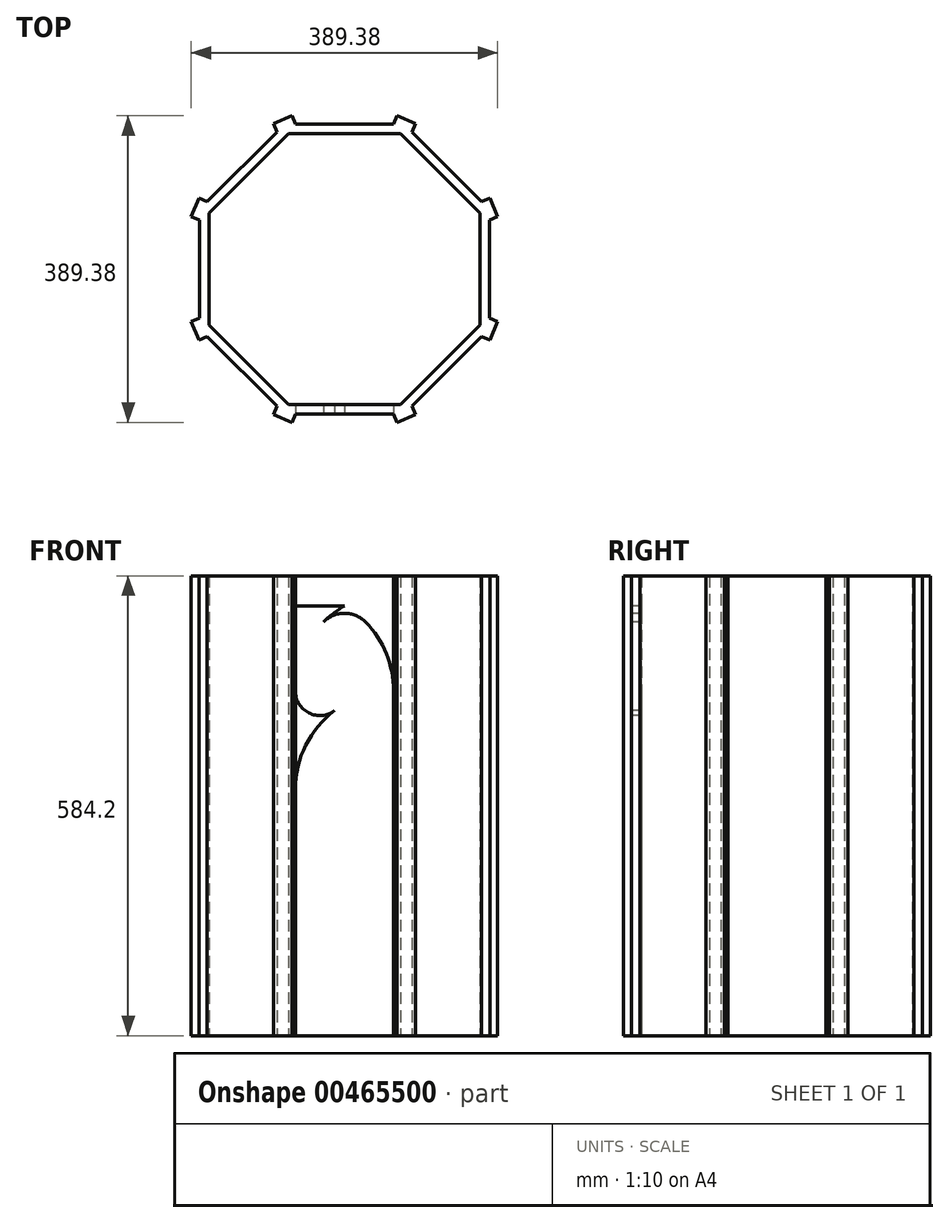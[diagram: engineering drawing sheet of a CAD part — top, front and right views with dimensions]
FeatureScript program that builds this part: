
annotation { "Feature Type Name" : "Feature", "Feature Type Description" : "" }
export const myFeature = defineFeature(function(context is Context, id is Id, definition is map)
    precondition{}
    {
        {
            var Q0;
            Q0=qCreatedBy(makeId("Top.planeOp"),FACE);
            var sketch = newSketch(context, id + "F0", { "sketchPlane" : qUnion([Q0])});
            skLineSegment(sketch, "E0.bottom", {"start": v(76.2, 183.96) * mm, "end": v(-76.2, 183.96) * mm});
            skLineSegment(sketch, "E0.top", {"start": v(76.2, -183.96) * mm, "end": v(-76.2, -183.96) * mm});
            skLineSegment(sketch, "E0.left", {"start": v(183.96, 76.2) * mm, "end": v(183.96, -76.2) * mm});
            skLineSegment(sketch, "E0.right", {"start": v(-183.96, 76.2) * mm, "end": v(-183.96, -76.2) * mm});
            skPoint(sketch, "E0.middle", {"position": v(0, 0) * mm});
            skLineSegment(sketch, "E1", {"start": v(-183.96, 76.2) * mm, "end": v(-76.2, 183.96) * mm});
            skLineSegment(sketch, "E2", {"start": v(-76.2, 183.96) * mm, "end": v(76.2, 183.96) * mm});
            skLineSegment(sketch, "E3", {"start": v(76.2, 183.96) * mm, "end": v(183.96, 76.2) * mm});
            skLineSegment(sketch, "E4", {"start": v(183.96, -76.2) * mm, "end": v(76.2, -183.96) * mm});
            skLineSegment(sketch, "E5", {"start": v(-76.2, -183.96) * mm, "end": v(-183.96, -76.2) * mm});
            skLineSegment(sketch, "E6", {"start": v(-183.96, -76.2) * mm, "end": v(-183.96, 76.2) * mm});
            skPoint(sketch, "E7.orphan", {"position": v(183.96, 183.96) * mm});
            skPoint(sketch, "E8.orphan", {"position": v(183.96, -183.96) * mm});
            skPoint(sketch, "E9.orphan", {"position": v(-183.96, -183.96) * mm});
            skLineSegment(sketch, "E10", {"start": v(-183.96, -62.45) * mm, "end": v(-194.69, -66.9) * mm});
            skLineSegment(sketch, "E11", {"start": v(-194.69, -66.9) * mm, "end": v(-184.97, -90.36) * mm});
            skLineSegment(sketch, "E12", {"start": v(-184.97, -90.36) * mm, "end": v(-174.24, -85.92) * mm});
            skLineSegment(sketch, "E13", {"start": v(-183.96, -76.2) * mm, "end": v(-224.47, -92.98) * mm, "construction": true});
            skPoint(sketch, "E14", {"position": v(-189.83, -78.63) * mm});
            skLineSegment(sketch, "E15.1.0", {"start": v(-184.97, 90.36) * mm, "end": v(-194.69, 66.9) * mm});
            skLineSegment(sketch, "E15.1.1", {"start": v(-194.69, 66.9) * mm, "end": v(-183.96, 62.45) * mm});
            skLineSegment(sketch, "E15.1.2", {"start": v(-174.24, 85.92) * mm, "end": v(-184.97, 90.36) * mm});
            skLineSegment(sketch, "E15.2.0", {"start": v(-66.9, 194.69) * mm, "end": v(-90.36, 184.97) * mm});
            skLineSegment(sketch, "E15.2.1", {"start": v(-90.36, 184.97) * mm, "end": v(-85.92, 174.24) * mm});
            skLineSegment(sketch, "E15.2.2", {"start": v(-62.45, 183.96) * mm, "end": v(-66.9, 194.69) * mm});
            skLineSegment(sketch, "E15.3.0", {"start": v(90.36, 184.97) * mm, "end": v(66.9, 194.69) * mm});
            skLineSegment(sketch, "E15.3.1", {"start": v(66.9, 194.69) * mm, "end": v(62.45, 183.96) * mm});
            skLineSegment(sketch, "E15.3.2", {"start": v(85.92, 174.24) * mm, "end": v(90.36, 184.97) * mm});
            skLineSegment(sketch, "E15.4.0", {"start": v(194.69, 66.9) * mm, "end": v(184.97, 90.36) * mm});
            skLineSegment(sketch, "E15.4.1", {"start": v(184.97, 90.36) * mm, "end": v(174.24, 85.92) * mm});
            skLineSegment(sketch, "E15.4.2", {"start": v(183.96, 62.45) * mm, "end": v(194.69, 66.9) * mm});
            skLineSegment(sketch, "E15.anchor1", {"start": v(-183.96, -63.21) * mm, "end": v(-194.69, -66.9) * mm, "construction": true});
            skPoint(sketch, "E16.orphan", {"position": v(-183.96, 183.96) * mm});
            skLineSegment(sketch, "E17.1.0", {"start": v(174.24, -85.92) * mm, "end": v(184.97, -90.36) * mm});
            skLineSegment(sketch, "E17.1.1", {"start": v(194.69, -66.9) * mm, "end": v(183.96, -62.45) * mm});
            skLineSegment(sketch, "E17.1.2", {"start": v(184.97, -90.36) * mm, "end": v(194.69, -66.9) * mm});
            skLineSegment(sketch, "E17.2.0", {"start": v(62.45, -183.96) * mm, "end": v(66.9, -194.69) * mm});
            skLineSegment(sketch, "E17.2.1", {"start": v(90.36, -184.97) * mm, "end": v(85.92, -174.24) * mm});
            skLineSegment(sketch, "E17.2.2", {"start": v(66.9, -194.69) * mm, "end": v(90.36, -184.97) * mm});
            skLineSegment(sketch, "E17.3.0", {"start": v(-85.92, -174.24) * mm, "end": v(-90.36, -184.97) * mm});
            skLineSegment(sketch, "E17.3.1", {"start": v(-66.9, -194.69) * mm, "end": v(-62.45, -183.96) * mm});
            skLineSegment(sketch, "E17.3.2", {"start": v(-90.36, -184.97) * mm, "end": v(-66.9, -194.69) * mm});
            skLineSegment(sketch, "E17.anchor1", {"start": v(0, 0) * mm, "end": v(174.24, 85.92) * mm, "construction": true});
            skLineSegment(sketch, "E17.anchor2", {"start": v(0, 0) * mm, "end": v(-62.45, -183.96) * mm, "construction": true});
            skLineSegment(sketch, "E18", {"start": v(-183.96, -62.45) * mm, "end": v(-174.24, -85.92) * mm});
            skLineSegment(sketch, "E19", {"start": v(-174.24, 85.92) * mm, "end": v(-183.96, 62.45) * mm});
            skLineSegment(sketch, "E20", {"start": v(-85.92, 174.24) * mm, "end": v(-62.45, 183.96) * mm});
            skLineSegment(sketch, "E21", {"start": v(62.45, 183.96) * mm, "end": v(85.92, 174.24) * mm});
            skLineSegment(sketch, "E22", {"start": v(174.24, 85.92) * mm, "end": v(183.96, 62.45) * mm});
            skLineSegment(sketch, "E23", {"start": v(183.96, -62.45) * mm, "end": v(174.24, -85.92) * mm});
            skLineSegment(sketch, "E24", {"start": v(85.92, -174.24) * mm, "end": v(62.45, -183.96) * mm});
            skLineSegment(sketch, "E25", {"start": v(-85.92, -174.24) * mm, "end": v(-62.45, -183.96) * mm});
            skLineSegment(sketch, "E26.0", {"start": v(-71.23, -171.96) * mm, "end": v(-171.96, -71.23) * mm});
            skLineSegment(sketch, "E26.1", {"start": v(71.23, -171.96) * mm, "end": v(-71.23, -171.96) * mm});
            skLineSegment(sketch, "E26.2", {"start": v(-171.96, -71.23) * mm, "end": v(-171.96, 71.23) * mm});
            skLineSegment(sketch, "E26.3", {"start": v(171.96, -71.23) * mm, "end": v(71.23, -171.96) * mm});
            skLineSegment(sketch, "E26.4", {"start": v(-171.96, 71.23) * mm, "end": v(-71.23, 171.96) * mm});
            skLineSegment(sketch, "E26.5", {"start": v(-71.23, 171.96) * mm, "end": v(71.23, 171.96) * mm});
            skLineSegment(sketch, "E26.6", {"start": v(71.23, 171.96) * mm, "end": v(171.96, 71.23) * mm});
            skLineSegment(sketch, "E26.7", {"start": v(171.96, 71.23) * mm, "end": v(171.96, -71.23) * mm});
            skSolve(sketch);
        }
        {
            var Q0;
            Q0=qCreatedBy(makeId("Front.planeOp"),FACE);
            cPlane(context, id + "F1", {"entities" : qUnion([Q0]), "cplaneType" : CPlaneType.OFFSET, "offset" : 183.97 * mm, "width" : 152.4 * mm, "height" : 152.4 * mm});
        }
        {
            var Q0;
            Q0=qCreatedBy(id+"F1.planeOp",FACE);
            var sketch = newSketch(context, id + "F2", { "sketchPlane" : qUnion([Q0])});
            skLineSegment(sketch, "E27.0", {"start": v(76.2, 0) * mm, "end": v(-76.2, 0) * mm});
            skPoint(sketch, "E27.1", {"position": v(-62.45, 0) * mm});
            skPoint(sketch, "E27.2", {"position": v(62.45, 0) * mm});
            skPoint(sketch, "E28.0", {"position": v(-66.9, 0) * mm});
            skPoint(sketch, "E29.0", {"position": v(66.9, 0) * mm});
            skLineSegment(sketch, "E30", {"start": v(-62.45, 0) * mm, "end": v(-62.45, 546.1) * mm});
            skLineSegment(sketch, "E31", {"start": v(-62.45, 546.1) * mm, "end": v(62.45, 546.1) * mm});
            skLineSegment(sketch, "E32", {"start": v(62.45, 546.1) * mm, "end": v(62.45, 0) * mm});
            skCircle(sketch, "E33", {"center": v(0, 546.1) * mm, "radius": 124.92 * mm, "construction": true});
            skArc(sketch, "E34", {"start": v(-62.45, 437.92) * mm, "mid": v(-45.71, 500.38) * mm, "end": v(0.02, 546.1) * mm});
            skArc(sketch, "E35", {"start": v(62.45, 437.92) * mm, "mid": v(45.71, 500.38) * mm, "end": v(-0.02, 546.1) * mm});
            skLineSegment(sketch, "E36", {"start": v(0, 437.92) * mm, "end": v(62.45, 437.92) * mm, "construction": true});
            skPoint(sketch, "E37", {"position": v(0, 437.92) * mm});
            skLineSegment(sketch, "E38", {"start": v(0, 437.92) * mm, "end": v(-62.45, 437.92) * mm, "construction": true});
            skPoint(sketch, "E39", {"position": v(-31.23, 437.92) * mm});
            skPoint(sketch, "E40", {"position": v(31.23, 437.92) * mm});
            skCircle(sketch, "E41", {"center": v(-31.23, 437.92) * mm, "radius": 31.23 * mm});
            skCircle(sketch, "E42", {"center": v(31.23, 437.92) * mm, "radius": 31.23 * mm});
            skCircle(sketch, "E43", {"center": v(0, 499.1) * mm, "radius": 37.47 * mm});
            skPoint(sketch, "E43.first.point", {"position": v(-26.77, 525.33) * mm});
            skPoint(sketch, "E43.second.point", {"position": v(26.77, 525.33) * mm});
            skPoint(sketch, "E43.third.point", {"position": v(-17.03, 465.73) * mm});
            skLineSegment(sketch, "E44", {"start": v(-62.45, 421.2) * mm, "end": v(62.45, 421.2) * mm, "construction": true});
            skPoint(sketch, "E44.endSnap0", {"position": v(62.45, 273.05) * mm});
            skCircle(sketch, "E45", {"center": v(0, 421.2) * mm, "radius": 124.92 * mm, "construction": true});
            skLineSegment(sketch, "E46", {"start": v(-62.45, 313) * mm, "end": v(62.45, 313) * mm, "construction": true});
            skArc(sketch, "E47", {"start": v(-62.45, 313) * mm, "mid": v(-45.71, 375.47) * mm, "end": v(0.02, 421.2) * mm});
            skArc(sketch, "E48", {"start": v(62.45, 313) * mm, "mid": v(45.72, 375.46) * mm, "end": v(0, 421.18) * mm});
            skLineSegment(sketch, "E49", {"start": v(62.45, 313) * mm, "end": v(124.91, 313) * mm, "construction": true});
            skLineSegment(sketch, "E50", {"start": v(-62.45, 313) * mm, "end": v(-124.91, 313) * mm, "construction": true});
            skArc(sketch, "E51", {"start": v(0, 313) * mm, "mid": v(-8.07, 357.17) * mm, "end": v(-31.23, 395.63) * mm});
            skArc(sketch, "E52", {"start": v(0, 313) * mm, "mid": v(8.07, 357.17) * mm, "end": v(31.23, 395.63) * mm});
            skSolve(sketch);
        }
        {
            var Q0;
            {var subQ3=sQuery(id+"F0.wireOp",EDGE,"E20");Q0=makeQuery(id+"F0.imprint","IMPRINT",FACE,{"disambiguationData":[TD([[makeQuery(id+"F0.imprint","IMPRINT",EDGE,{"derivedFrom":subQ3}),1.0]])]});}
            var Q1;
            {var subQ3=sQuery(id+"F0.wireOp",EDGE,"E25");Q1=makeQuery(id+"F0.imprint","IMPRINT",FACE,{"disambiguationData":[TD([[makeQuery(id+"F0.imprint","IMPRINT",EDGE,{"derivedFrom":subQ3}),-1.0]])]});}
            var Q2;
            {var subQ1=sQuery(id+"F0.wireOp",EDGE,"E17.2.0");Q2=makeQuery(id+"F0.imprint","IMPRINT",FACE,{"disambiguationData":[TD([[makeQuery(id+"F0.imprint","IMPRINT",EDGE,{"derivedFrom":subQ1}),1.0]])]});}
            var Q3;
            Q3=makeQuery(id+"F0.imprint","IMPRINT",FACE,{"disambiguationData":[TD([[makeQuery(id+"F0.imprint","IMPRINT",EDGE,{"derivedFrom":sQuery(id+"F0.wireOp",EDGE,"E15.3.0")}),1.0]])]});
            var Q4;
            Q4=makeQuery(id+"F0.imprint","IMPRINT",FACE,{"disambiguationData":[TD([[makeQuery(id+"F0.imprint","IMPRINT",EDGE,{"derivedFrom":sQuery(id+"F0.wireOp",EDGE,"E15.1.0")}),1.0]])]});
            var Q5;
            {var subQ3=sQuery(id+"F0.wireOp",EDGE,"E21");Q5=makeQuery(id+"F0.imprint","IMPRINT",FACE,{"disambiguationData":[TD([[makeQuery(id+"F0.imprint","IMPRINT",EDGE,{"derivedFrom":subQ3}),1.0]])]});}
            var Q6;
            {var subQ3=sQuery(id+"F0.wireOp",EDGE,"E23");Q6=makeQuery(id+"F0.imprint","IMPRINT",FACE,{"disambiguationData":[TD([[makeQuery(id+"F0.imprint","IMPRINT",EDGE,{"derivedFrom":subQ3}),1.0]])]});}
            var Q7;
            {var subQ0=sQuery(id+"F0.wireOp",EDGE,"E10");Q7=makeQuery(id+"F0.imprint","IMPRINT",FACE,{"disambiguationData":[TD([[makeQuery(id+"F0.imprint","IMPRINT",EDGE,{"derivedFrom":subQ0}),1.0]])]});}
            var Q8;
            {var subQ1=sQuery(id+"F0.wireOp",EDGE,"E17.3.0");Q8=makeQuery(id+"F0.imprint","IMPRINT",FACE,{"disambiguationData":[TD([[makeQuery(id+"F0.imprint","IMPRINT",EDGE,{"derivedFrom":subQ1}),1.0]])]});}
            var Q9;
            {var subQ10=sQuery(id+"F0.wireOp",EDGE,"E18");Q9=makeQuery(id+"F0.imprint","IMPRINT",FACE,{"disambiguationData":[TD([[makeQuery(id+"F0.imprint","IMPRINT",EDGE,{"derivedFrom":subQ10}),1.0]])]});}
            var Q10;
            {var subQ3=sQuery(id+"F0.wireOp",EDGE,"E18");Q10=makeQuery(id+"F0.imprint","IMPRINT",FACE,{"disambiguationData":[TD([[makeQuery(id+"F0.imprint","IMPRINT",EDGE,{"derivedFrom":subQ3}),-1.0]])]});}
            var Q11;
            {var subQ3=sQuery(id+"F0.wireOp",EDGE,"E22");Q11=makeQuery(id+"F0.imprint","IMPRINT",FACE,{"disambiguationData":[TD([[makeQuery(id+"F0.imprint","IMPRINT",EDGE,{"derivedFrom":subQ3}),1.0]])]});}
            var Q12;
            Q12=makeQuery(id+"F0.imprint","IMPRINT",FACE,{"disambiguationData":[TD([[makeQuery(id+"F0.imprint","IMPRINT",EDGE,{"derivedFrom":sQuery(id+"F0.wireOp",EDGE,"E15.4.0")}),1.0]])]});
            var Q13;
            Q13=makeQuery(id+"F0.imprint","IMPRINT",FACE,{"disambiguationData":[TD([[makeQuery(id+"F0.imprint","IMPRINT",EDGE,{"derivedFrom":sQuery(id+"F0.wireOp",EDGE,"E15.2.0")}),1.0]])]});
            var Q14;
            {var subQ3=sQuery(id+"F0.wireOp",EDGE,"E24");Q14=makeQuery(id+"F0.imprint","IMPRINT",FACE,{"disambiguationData":[TD([[makeQuery(id+"F0.imprint","IMPRINT",EDGE,{"derivedFrom":subQ3}),1.0]])]});}
            var Q15;
            {var subQ3=sQuery(id+"F0.wireOp",EDGE,"E19");Q15=makeQuery(id+"F0.imprint","IMPRINT",FACE,{"disambiguationData":[TD([[makeQuery(id+"F0.imprint","IMPRINT",EDGE,{"derivedFrom":subQ3}),-1.0]])]});}
            var Q16;
            {var subQ1=sQuery(id+"F0.wireOp",EDGE,"E17.1.0");Q16=makeQuery(id+"F0.imprint","IMPRINT",FACE,{"disambiguationData":[TD([[makeQuery(id+"F0.imprint","IMPRINT",EDGE,{"derivedFrom":subQ1}),1.0]])]});}
            extrude(context, id + "F3", {"entities" : qUnion([Q0, Q1, Q2, Q3, Q4, Q5, Q6, Q7, Q8, Q9, Q10, Q11, Q12, Q13, Q14, Q15, Q16]), "depth" : 584.2 * mm});
        }
        {
            var Q0;
            {var subQ1=sQuery(id+"F2.wireOp",EDGE,"E30");var subQ3=sQuery(id+"F2.wireOp",EDGE,"E47");var subQ4=makeQuery(id+"F2.imprint","INTERSECT",VERTEX,{"derivedFrom":[subQ1,subQ3]});Q0=makeQuery(id+"F2.imprint","IMPRINT",FACE,{"disambiguationData":[TD([[makeQuery(id+"F2.imprint","IMPRINT",EDGE,{"disambiguationData":[TD([[subQ4,-1.0]])],"derivedFrom":subQ3}),1.0]])]});}
            var Q1;
            {var subQ0=sQuery(id+"F2.wireOp",EDGE,"E43");var subQ1=sQuery(id+"F2.wireOp",EDGE,"E41");var subQ2=makeQuery(id+"F2.imprint","INTERSECT",VERTEX,{"derivedFrom":[subQ1,subQ0]});Q1=makeQuery(id+"F2.imprint","IMPRINT",FACE,{"disambiguationData":[TD([[makeQuery(id+"F2.imprint","IMPRINT",EDGE,{"disambiguationData":[TD([[subQ2,1.0]])],"derivedFrom":subQ1}),-1.0]])]});}
            var Q2;
            {var subQ0=sQuery(id+"F2.wireOp",EDGE,"E43");var subQ1=sQuery(id+"F2.wireOp",EDGE,"E34");var subQ2=makeQuery(id+"F2.imprint","INTERSECT",VERTEX,{"derivedFrom":[subQ1,subQ0]});Q2=makeQuery(id+"F2.imprint","IMPRINT",FACE,{"disambiguationData":[TD([[makeQuery(id+"F2.imprint","IMPRINT",EDGE,{"disambiguationData":[TD([[subQ2,-1.0]])],"derivedFrom":subQ1}),-1.0]])]});}
            var Q3;
            {var subQ1=sQuery(id+"F2.wireOp",EDGE,"E34");var subQ3=sQuery(id+"F2.wireOp",EDGE,"E43");var subQ4=makeQuery(id+"F2.imprint","INTERSECT",VERTEX,{"derivedFrom":[subQ1,subQ3]});Q3=makeQuery(id+"F2.imprint","IMPRINT",FACE,{"disambiguationData":[TD([[makeQuery(id+"F2.imprint","IMPRINT",EDGE,{"disambiguationData":[TD([[subQ4,-1.0]])],"derivedFrom":subQ3}),-1.0]])]});}
            var Q4;
            {var subQ0=sQuery(id+"F2.wireOp",EDGE,"E43");var subQ1=makeQuery(id+"F2.imprint","INTERSECT",VERTEX,{"derivedFrom":[sQuery(id+"F2.wireOp",EDGE,"E34"),subQ0]});Q4=makeQuery(id+"F2.imprint","IMPRINT",FACE,{"disambiguationData":[TD([[makeQuery(id+"F2.imprint","IMPRINT",EDGE,{"disambiguationData":[TD([[subQ1,1.0]])],"derivedFrom":subQ0}),1.0]])]});}
            var Q5;
            {var subQ0=sQuery(id+"F2.wireOp",EDGE,"E42");var subQ3=makeQuery(id+"F2.imprint","INTERSECT",VERTEX,{"derivedFrom":[sQuery(id+"F2.wireOp",EDGE,"E41"),subQ0]});Q5=makeQuery(id+"F2.imprint","IMPRINT",FACE,{"disambiguationData":[TD([[makeQuery(id+"F2.imprint","IMPRINT",EDGE,{"disambiguationData":[TD([[subQ3,1.0]])],"derivedFrom":subQ0}),1.0]])]});}
            var Q6;
            {var subQ1=sQuery(id+"F2.wireOp",EDGE,"E35");var subQ3=sQuery(id+"F2.wireOp",EDGE,"E43");var subQ4=makeQuery(id+"F2.imprint","INTERSECT",VERTEX,{"derivedFrom":[subQ1,subQ3]});Q6=makeQuery(id+"F2.imprint","IMPRINT",FACE,{"disambiguationData":[TD([[makeQuery(id+"F2.imprint","IMPRINT",EDGE,{"disambiguationData":[TD([[subQ4,1.0]])],"derivedFrom":subQ3}),-1.0]])]});}
            var Q7;
            {var subQ6=sQuery(id+"F2.wireOp",EDGE,"E51");Q7=makeQuery(id+"F2.imprint","IMPRINT",FACE,{"disambiguationData":[TD([[makeQuery(id+"F2.imprint","IMPRINT",EDGE,{"derivedFrom":subQ6}),-1.0]])]});}
            var Q8;
            {var subQ0=sQuery(id+"F2.wireOp",EDGE,"E41");var subQ1=makeQuery(id+"F2.imprint","INTERSECT",VERTEX,{"derivedFrom":[subQ0,sQuery(id+"F2.wireOp",EDGE,"E43")]});Q8=makeQuery(id+"F2.imprint","IMPRINT",FACE,{"disambiguationData":[TD([[makeQuery(id+"F2.imprint","IMPRINT",EDGE,{"disambiguationData":[TD([[subQ1,1.0]])],"derivedFrom":subQ0}),1.0]])]});}
            var Q9;
            {var subQ1=sQuery(id+"F2.wireOp",EDGE,"E32");var subQ3=sQuery(id+"F2.wireOp",EDGE,"E48");var subQ4=makeQuery(id+"F2.imprint","INTERSECT",VERTEX,{"derivedFrom":[subQ1,subQ3]});Q9=makeQuery(id+"F2.imprint","IMPRINT",FACE,{"disambiguationData":[TD([[makeQuery(id+"F2.imprint","IMPRINT",EDGE,{"disambiguationData":[TD([[subQ4,-1.0]])],"derivedFrom":subQ3}),-1.0]])]});}
            var Q10;
            {var subQ0=sQuery(id+"F2.wireOp",EDGE,"E42");var subQ1=sQuery(id+"F2.wireOp",EDGE,"E41");var subQ2=makeQuery(id+"F2.imprint","INTERSECT",VERTEX,{"derivedFrom":[subQ1,subQ0]});Q10=makeQuery(id+"F2.imprint","IMPRINT",FACE,{"disambiguationData":[TD([[makeQuery(id+"F2.imprint","IMPRINT",EDGE,{"disambiguationData":[TD([[subQ2,1.0]])],"derivedFrom":subQ1}),-1.0]])]});}
            var Q11;
            {var subQ3=sQuery(id+"F2.wireOp",EDGE,"E51");Q11=makeQuery(id+"F2.imprint","IMPRINT",FACE,{"disambiguationData":[TD([[makeQuery(id+"F2.imprint","IMPRINT",EDGE,{"derivedFrom":subQ3}),1.0]])]});}
            extrude(context, id + "F4", {"entities" : qUnion([Q0, Q1, Q2, Q3, Q4, Q5, Q6, Q7, Q8, Q9, Q10, Q11]), "operationType" : NewBodyOperationType.REMOVE, "oppositeDirection" : true, "depth" : 25.4 * mm});
        }
    });
